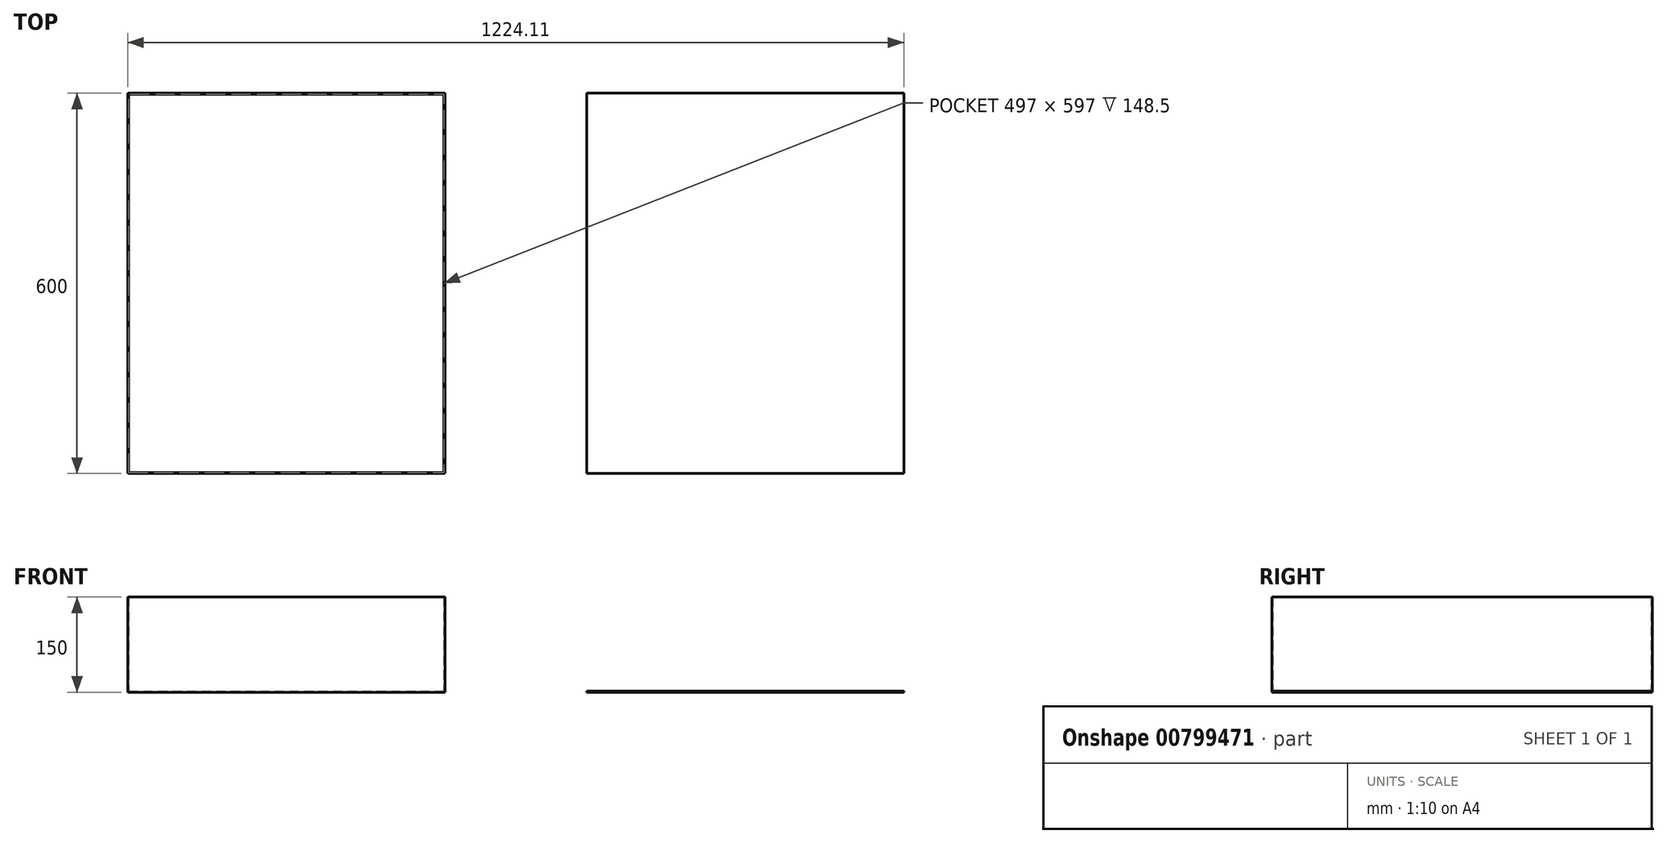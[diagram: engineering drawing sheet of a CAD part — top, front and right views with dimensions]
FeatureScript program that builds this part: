
annotation { "Feature Type Name" : "Feature", "Feature Type Description" : "" }
export const myFeature = defineFeature(function(context is Context, id is Id, definition is map)
    precondition{}
    {
        {
            var Q0;
            Q0=qCreatedBy(makeId("Top.planeOp"),FACE);
            var sketch = newSketch(context, id + "F0", { "sketchPlane" : qUnion([Q0])});
            skLineSegment(sketch, "E0.bottom", {"start": v(0, 0) * mm, "end": v(500, 0) * mm});
            skLineSegment(sketch, "E0.top", {"start": v(0, 600) * mm, "end": v(500, 600) * mm});
            skLineSegment(sketch, "E0.left", {"start": v(0, 0) * mm, "end": v(0, 600) * mm});
            skLineSegment(sketch, "E0.right", {"start": v(500, 0) * mm, "end": v(500, 600) * mm});
            skLineSegment(sketch, "E1.bottom", {"start": v(724.1, 0) * mm, "end": v(1224.1, 0) * mm});
            skLineSegment(sketch, "E1.top", {"start": v(724.1, 600) * mm, "end": v(1224.1, 600) * mm});
            skLineSegment(sketch, "E1.left", {"start": v(724.1, 0) * mm, "end": v(724.1, 600) * mm});
            skLineSegment(sketch, "E1.right", {"start": v(1224.1, 0) * mm, "end": v(1224.1, 600) * mm});
            skSolve(sketch);
        }
        {
            var Q0;
            Q0=makeQuery(id+"F0.imprint","IMPRINT",FACE,{"disambiguationData":[TD([[makeQuery(id+"F0.imprint","IMPRINT",EDGE,{"derivedFrom":sQuery(id+"F0.wireOp",EDGE,"E0.bottom")}),1.0]])]});
            extrude(context, id + "F1", {"entities" : qUnion([Q0]), "depth" : 150 * mm, "offsetDistance" : 25 * mm});
        }
        {
            var Q0;
            Q0=makeQuery(id+"F1.opExtrude","CAP_FACE",FACE,{"disambiguationData":[OSD([sQuery(id+"F0.wireOp",EDGE,"E0.bottom"),sQuery(id+"F0.wireOp",EDGE,"E0.top"),sQuery(id+"F0.wireOp",EDGE,"E0.left"),sQuery(id+"F0.wireOp",EDGE,"E0.right")])],"isStart":false});
            shell(context, id + "F2", {"entities" : qUnion([Q0]), "thickness" : 1.5 * mm});
        }
        {
            var Q0;
            Q0=makeQuery(id+"F0.imprint","IMPRINT",FACE,{"disambiguationData":[TD([[makeQuery(id+"F0.imprint","IMPRINT",EDGE,{"derivedFrom":sQuery(id+"F0.wireOp",EDGE,"E1.bottom")}),1.0]])]});
            extrude(context, id + "F3", {"entities" : qUnion([Q0]), "depth" : 1.5 * mm, "offsetDistance" : 25 * mm});
        }
    });
